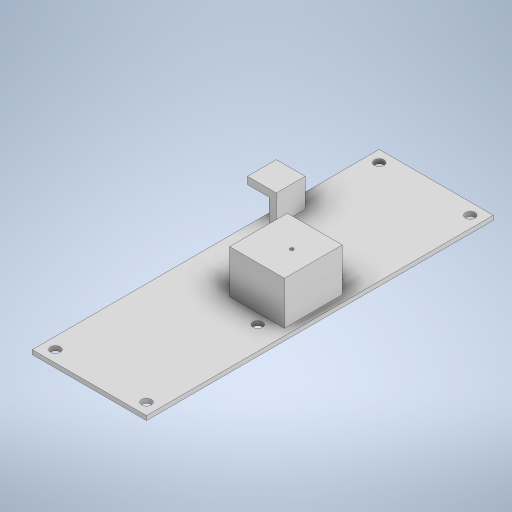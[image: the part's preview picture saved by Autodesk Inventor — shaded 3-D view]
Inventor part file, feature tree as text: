
AUTODESK INVENTOR PART (.ipt)
format: ipt  version: 2023 (Build 270158000, 158)  size: 343,040 bytes
history: native  units: mm
features: extrude x12, sketch x12
ambient origin geometry x8: Origin, YZ Plane, XZ Plane, XY Plane, X Axis, Y Axis, Z Axis, Center Point
bodies: Body1 (feature_tree)
feature tree (24):
  extrude  "Extrusion33"  Depth=240.0mm
  extrude  "Extrusion34"  Depth=38.0mm
  extrude  "Extrusion35"  Depth=30.0mm TaperAngle=0.0deg
  extrude  "Extrusion38"  Depth=30.0mm
  extrude  "Extrusion39"  Depth=15.0mm
  extrude  "Extrusion40"  Depth=3.5mm
  extrude  "Extrusion41"  Depth=35.0mm TaperAngle=0.0deg
  extrude  "Extrusion43"  Depth=20.0mm
  extrude  "Extrusion46"  Depth=20.0mm
  extrude  "Extrusion47"  Depth=5.0mm TaperAngle=0.0deg
  extrude  "Extrusion48"  Depth=10.0mm TaperAngle=0.0deg
  extrude  "Extrusion51"  Depth=10.0mm
  sketch  "Sketch44"  dims[d138=79.0mm d139=240.0mm]
  sketch  "Sketch45"  dims[d140=3.0mm d141=0.0mm d142=38.0mm]
  sketch  "Sketch47"  dims[d143=40.0mm d144=30.0mm d145=0.0mm]
  sketch  "Sketch58"  dims[d146=36.0mm d147=30.0mm d148=-2.617994mm]
  sketch  "Sketch59"  dims[d156=20.0mm d157=15.0mm]
  sketch  "Sketch60"  dims[d158=15.0mm d159=0.0mm d160=3.5mm]
  sketch  "Sketch61"  dims[d161=20.0mm d162=35.0mm d163=0.0mm]
  sketch  "Sketch65"  dims[d164=5.0mm d165=20.0mm]
  sketch  "Sketch68"  dims[d166=20.0mm d167=0.0mm d168=20.0mm]
  sketch  "Sketch69"  dims[d169=20.0mm d170=5.0mm d171=0.0mm]
  sketch  "Sketch70"  dims[d176=6.0mm d177=10.0mm d178=0.0mm]
  sketch  "Sketch74"  dims[d192=6.7mm d193=6.7mm d194=6.7mm d195=6.7mm d196=10.0mm d197=0.0mm d198=6.7mm d199=6.7mm d200=10.0mm d201=0.0mm d202=8.0mm d203=0.0mm d210=2.3mm d211=10.0mm d212=0.0mm d49=0.5mm d50=0.872665mm d51=0.5mm d52=0.872665mm d130=0.5mm d131=0.872665mm d132=0.5mm d133=0.872665mm d173=0.5mm d174=0.872665mm d175=0.5mm]
